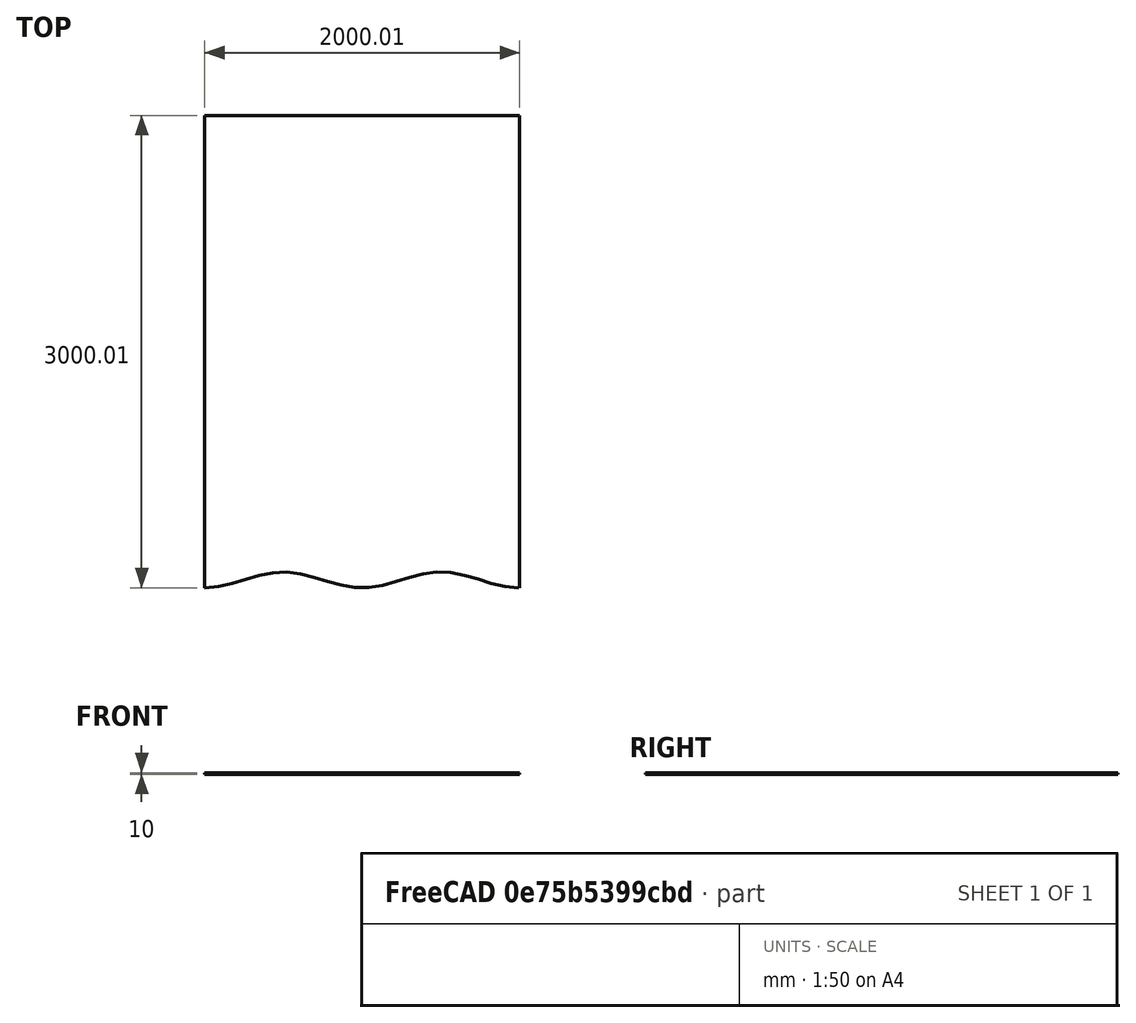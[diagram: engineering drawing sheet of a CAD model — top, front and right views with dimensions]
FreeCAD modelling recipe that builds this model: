
FCSTD DOCUMENT  (FreeCAD 0.19R24291 (Git))
Label: cosineSurface
License: All rights reserved
LicenseURL: http://en.wikipedia.org/wiki/All_rights_reserved
objects: Part::Extrusion×2, Part::Part2DObjectPython×1, Sketcher::SketchObject×1, App::Part×1
note: 4 computed .brp shape members not serialized (recipe doc carries the construction recipe); baked Part::Feature solids carry a one-line shape summary decoded from their .brp

FEATURE [Part::Part2DObjectPython] BSpline  # Draft 2D object (typed FeaturePython)
  Area = 0
  Closed = false
  MakeFace = true
  Parameterization = 1
  Points = (360) [(-1000,-50,0),(-994.444,-49.9695,0),(-988.889,-49.8782,0),(-983.333,-49.7261,0),(-977.778,-49.5134,0),(-972.222,-49.2404,0),(-966.667,-48.9074,0),+353 more]
FEATURE [Sketcher::SketchObject] Sketch
  FullyConstrained = true
  MapMode = 9
  Placement = pos=(-1000,-50,0) rot=(0,0,-1;5e-06rad)
  Support = -> [BSpline]
  sketch-geometry (3):
    g0: LineSegment StartX=0 StartY=0 StartZ=0 EndX=0 EndY=3000 EndZ=0
    g1: LineSegment StartX=0 StartY=3000 StartZ=0 EndX=2000 EndY=3000 EndZ=0
    g2: LineSegment StartX=2000 StartY=3000 StartZ=0 EndX=2000 EndY=4.547e-13 EndZ=0
  constraints (9):
    c: Coincident(g0,g-1)
    c: Vertical(g0)
    c: Coincident(g1,g0)
    c: Horizontal(g1)
    c: DistanceY(g0,g0) = 3000
    c: DistanceX(g1,g1) = 2000
    c: Coincident(g2,g1)
    c: Vertical(g2)
    c: DistanceY(g2,g2) = 3000
FEATURE [App::Part] Part
  Origin = -> Origin
FEATURE [Part::Extrusion] Extrude
  Base = -> Sketch
  Dir = (0,0,1)
  DirMode = 2
  FaceMakerClass = Part::FaceMakerBullseye
  LengthFwd = 10
  LengthRev = 0
  Solid = false
  Symmetric = false
FEATURE [Part::Extrusion] Extrude001
  Base = -> BSpline
  Dir = (0,0,1)
  DirMode = 2
  FaceMakerClass = Part::FaceMakerBullseye
  LengthFwd = 10
  LengthRev = 0
  Solid = false
  Symmetric = false
